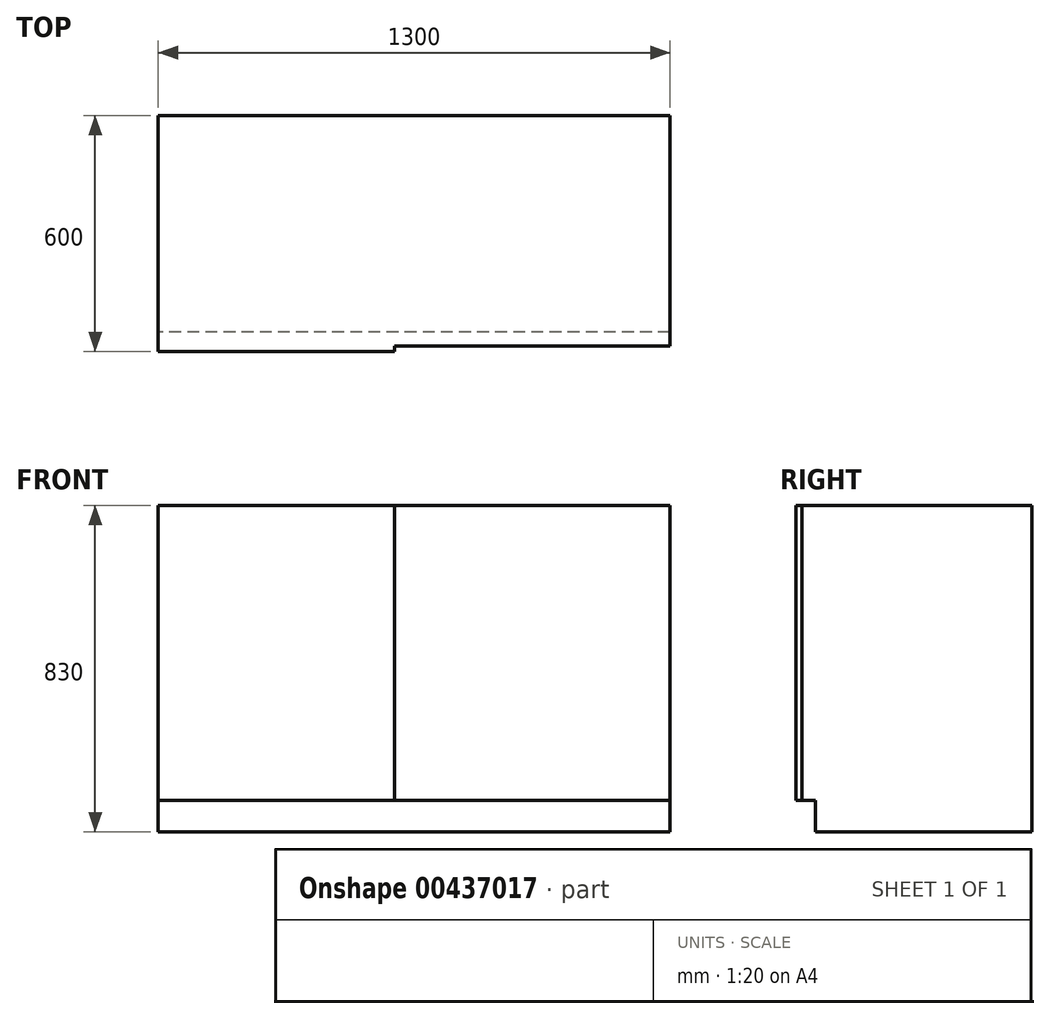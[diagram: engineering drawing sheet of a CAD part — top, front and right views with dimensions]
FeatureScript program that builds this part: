
annotation { "Feature Type Name" : "Feature", "Feature Type Description" : "" }
export const myFeature = defineFeature(function(context is Context, id is Id, definition is map)
    precondition{}
    {
        {
            var Q0;
            Q0=qCreatedBy(makeId("Right.planeOp"),FACE);
            var sketch = newSketch(context, id + "F0", { "sketchPlane" : qUnion([Q0])});
            skLineSegment(sketch, "E0.bottom", {"start": v(0, 0) * mm, "end": v(-550, 0) * mm});
            skLineSegment(sketch, "E0.top", {"start": v(0, 830) * mm, "end": v(-600, 830) * mm});
            skLineSegment(sketch, "E0.left", {"start": v(0, 0) * mm, "end": v(0, 830) * mm});
            skLineSegment(sketch, "E0.right", {"start": v(-600, 80) * mm, "end": v(-600, 830) * mm});
            skLineSegment(sketch, "E1.top", {"start": v(-600, 80) * mm, "end": v(-550, 80) * mm});
            skLineSegment(sketch, "E1.right", {"start": v(-550, 0) * mm, "end": v(-550, 80) * mm});
            skSolve(sketch);
        }
        {
            var Q0;
            Q0=qSketchRegion(id+"F0",true);
            extrude(context, id + "F1", {"entities" : qUnion([Q0]), "depth" : 1300 * mm});
        }
        {
            var Q0;
            Q0=makeQuery(id+"F1.opExtrude","SWEPT_FACE",FACE,{"disambiguationData":[OSD([sQuery(id+"F0.wireOp",EDGE,"E0.top")])]});
            var sketch = newSketch(context, id + "F2", { "sketchPlane" : qUnion([Q0])});
            skLineSegment(sketch, "E2.bottom", {"start": v(1300, -600) * mm, "end": v(600, -600) * mm});
            skLineSegment(sketch, "E2.top", {"start": v(1300, -585) * mm, "end": v(600, -585) * mm});
            skLineSegment(sketch, "E2.left", {"start": v(1300, -600) * mm, "end": v(1300, -585) * mm});
            skLineSegment(sketch, "E2.right", {"start": v(600, -600) * mm, "end": v(600, -585) * mm});
            skSolve(sketch);
        }
        {
            var Q0;
            Q0 = qSketchRegion(id + "F2", true);
            extrude(context, id + "F3", {"entities" : qUnion([Q0]), "operationType" : NewBodyOperationType.REMOVE, "endBound" : BoundingType.THROUGH_ALL, "oppositeDirection" : true, "depth" : 25 * mm});
        }
    });
